# Revit family: Комби-клапан – регулятор расхода 4206_M_SMART
name_source: partatom
category: Rohrzubehör
revit_build: Autodesk Revit 2018 (Build: 20190510_1515(x64)
units: mm (PartAtom-declared; Revit-internal decimal feet)

## family parameters
Arbeitsebenenbasiert = Nein
Beim Laden mit Abzugskörper schneiden = Nein
Bemaßung runder Anschluss = Durchmesser verwenden
Gemeinsam genutzt = Nein
Immer vertikal = Ja
OmniClass-Nummer = 23.65.55.14
OmniClass-Titel = Valves for Liquid Services
Teiletyp = Unterbricht

## types (1)
- Комби-клапан – регулятор расхода 4206_M_SMART
    B01 = 41.62 mm  [stored 0.136549 ft]
    B03 = 7.93 mm  [stored 0.0260171 ft]
    B04 = 6.75 mm  [stored 0.0221457 ft]
    B05 = 3.7 mm  [stored 0.0121391 ft]
    B06 = 5.86 mm  [stored 0.0192257 ft]
    B08 = 23.05 mm  [stored 0.0756234 ft]
    B10 = 31.75 mm
    B11 = 34.69 mm
    B12 = 36.73 mm
    B13 = 40.79 mm  [stored 0.133825 ft]
    B14 = 8.73 mm  [stored 0.0286417 ft]
    B15 = 23 mm  [stored 0.0754593 ft]
    H01 = 35 mm  [stored 0.114829 ft]
    H03 = 3.46 mm  [stored 0.0113517 ft]
    H04 = 6.74 mm  [stored 0.0221129 ft]
    H05 = 10.06 mm  [stored 0.0330052 ft]
    H06 = 24.02 mm  [stored 0.0788058 ft]
    H07 = 28.19 mm  [stored 0.0924869 ft]
    H08 = 4.24 mm
    H09 = 1.08 mm
    H10 = 22.33 mm  [stored 0.0732612 ft]
    Hersteller = Herz-Armaturen GmbH
    L01 = 41 mm  [stored 0.134514 ft]
    L02 = 34 mm
    L05 = 3.44 mm  [stored 0.0112861 ft]
    L06 = 3.44 mm  [stored 0.0112861 ft]
    L13 = 32 mm  [stored 0.104987 ft]
    L14 = 44 mm  [stored 0.144357 ft]
    PN = 25
    SCRNCODE = 05;04;02
    SCRNSEQ = ARM;ARM_TYP="DURR";2
    URL = www.herz-armaturen.ru
    Защитный колпачок = Пластик
    Импульсная трубка = Медь Cu-DHP (CW024A)
    Кольцевое уплотнение O-Ring = EPDM
    Корпус = Латунь, устойчивая к селективной цинковой коррозии
    Корпус мембраны = Латунь CW602N
    Макс. перепад давления = 400000.0 Pa
    Макс. рабочая температура до DN32 = 130 °C
    Макс. рабочая температура от DN40 = 110 °C
    Макс. рабочее давление = 1600000.0 Pa
    Мембрана = EPDM
    Мин. рабочая температура (антифриз) = -20 °C
    Мин. рабочая температура (чистая вода) = 2 °C
    Область применения = Комби-клапан применяется в системах отопления и охлаждения с насосами. Комби-клапан автоматически ограничивает расход на выбранном участке системы до заданного значения, компенсируя все колебания давления. При этом нет необходимости в измерениях, а регулирование эффективно при любых условиях эксплуатации. Комби-клапан регулирует расход в соответствии с настройкой до заданного значения; на мембрану воздействует давление непосредственно до и после регулирующей части.
    Пружина = Пружинная нержавеющая сталь
    Среда = Качество теплоносителя в соответствии с ÖNORM H5195 и/или предписаниями VDI-Standard 2035.
Разрешается использование смеси этилен- или пропиленгликоля в соотношении 25-50% с водой.
    Ход = 4 mm  [stored 0.0131234 ft]
    Шпиндель = Нержавеющая сталь 14301

note: [stored X ft] marks values corroborated as IEEE doubles in the binary element streams (Revit-internal decimal feet)
